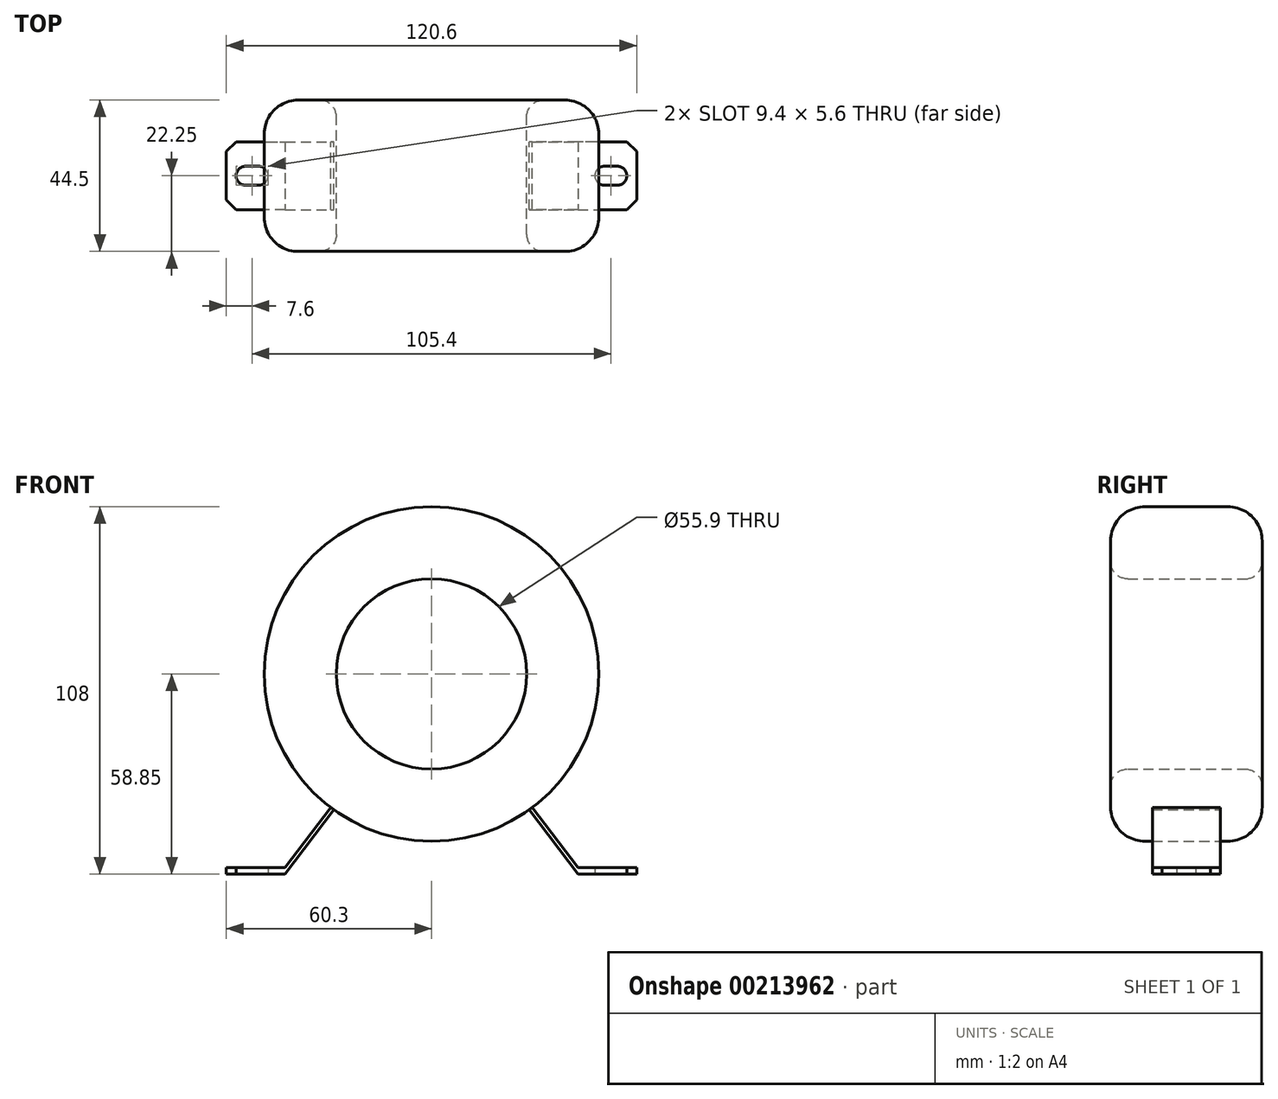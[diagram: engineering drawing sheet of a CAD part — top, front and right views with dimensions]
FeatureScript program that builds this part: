
annotation { "Feature Type Name" : "Feature", "Feature Type Description" : "" }
export const myFeature = defineFeature(function(context is Context, id is Id, definition is map)
    precondition{}
    {
        {
            var Q0;
            Q0=qCreatedBy(makeId("Front.planeOp"),FACE);
            var sketch = newSketch(context, id + "F0", { "sketchPlane" : qUnion([Q0])});
            skCircle(sketch, "E0", {"center": v(0, 49.15) * mm, "radius": 27.95 * mm});
            skCircle(sketch, "E1", {"center": v(0, 49.15) * mm, "radius": 49.15 * mm});
            skPoint(sketch, "E2", {"position": v(0, 0) * mm});
            skPoint(sketch, "E3", {"position": v(0, 21.2) * mm});
            skLineSegment(sketch, "E4", {"start": v(-76.83, -9.7) * mm, "end": v(67.55, -9.7) * mm});
            skSolve(sketch);
        }
        {
            var Q0;
            Q0=makeQuery(id+"F0.imprint","IMPRINT",FACE,{"disambiguationData":[TD([[makeQuery(id+"F0.imprint","IMPRINT",EDGE,{"derivedFrom":sQuery(id+"F0.wireOp",EDGE,"E0")}),-1.0]])]});
            extrude(context, id + "F1", {"entities" : qUnion([Q0]), "endBound" : BoundingType.SYMMETRIC, "depth" : 44.5 * mm});
        }
        {
            var Q0;
            Q0=makeQuery(id+"F1.opExtrude","CAP_EDGE",EDGE,{"disambiguationData":[OSD([sQuery(id+"F0.wireOp",EDGE,"E1")])],"isStart":false});
            var Q1;
            Q1=makeQuery(id+"F1.opExtrude","CAP_EDGE",EDGE,{"disambiguationData":[OSD([sQuery(id+"F0.wireOp",EDGE,"E1")])],"isStart":true});
            fillet(context, id + "F2", {"entities" : qUnion([Q0, Q1]), "radius" : 10 * mm, "tangentPropagation" : true, "allowEdgeOverflow" : false});
        }
        {
            var Q0;
            Q0=makeQuery(id+"F1.opExtrude","CAP_EDGE",EDGE,{"disambiguationData":[OSD([sQuery(id+"F0.wireOp",EDGE,"E0")])],"isStart":true});
            var Q1;
            Q1=makeQuery(id+"F1.opExtrude","CAP_EDGE",EDGE,{"disambiguationData":[OSD([sQuery(id+"F0.wireOp",EDGE,"E0")])],"isStart":false});
            fillet(context, id + "F3", {"entities" : qUnion([Q0, Q1]), "radius" : 5 * mm, "tangentPropagation" : true, "allowEdgeOverflow" : false});
        }
        {
            var Q0;
            Q0=sQuery(id+"F0.wireOp",EDGE,"E4");
            extrude(context, id + "F4", {"bodyType" : ToolBodyType.SURFACE, "surfaceEntities" : qUnion([Q0]), "endBound" : BoundingType.SYMMETRIC, "depth" : 25 * mm});
        }
        {
            var Q0;
            Q0=makeQuery(id+"F4.opExtrude","SWEPT_FACE",FACE,{"disambiguationData":[OSD([sQuery(id+"F0.wireOp",EDGE,"E4")])]});
            var sketch = newSketch(context, id + "F5", { "sketchPlane" : qUnion([Q0])});
            skLineSegment(sketch, "E5", {"start": v(0, -24.95) * mm, "end": v(0, 24.95) * mm, "construction": true});
            skLineSegment(sketch, "E6", {"start": v(-57.4, 0) * mm, "end": v(57.4, 0) * mm, "construction": true});
            skLineSegment(sketch, "E7", {"start": v(43, -10) * mm, "end": v(43, 10) * mm});
            skLineSegment(sketch, "E8", {"start": v(43, 10) * mm, "end": v(57.4, 10) * mm});
            skLineSegment(sketch, "E9", {"start": v(57.4, 10) * mm, "end": v(60.3, 7.1) * mm});
            skLineSegment(sketch, "E10", {"start": v(60.3, 7.1) * mm, "end": v(60.3, -7.1) * mm});
            skLineSegment(sketch, "E11", {"start": v(60.3, -7.1) * mm, "end": v(57.4, -10) * mm});
            skLineSegment(sketch, "E12", {"start": v(57.4, -10) * mm, "end": v(43, -10) * mm});
            skCircle(sketch, "E13", {"center": v(54.6, 0) * mm, "radius": 2.8 * mm});
            skCircle(sketch, "E14", {"center": v(50.8, 0) * mm, "radius": 2.8 * mm});
            skLineSegment(sketch, "E15", {"start": v(50.8, -2.8) * mm, "end": v(54.6, -2.8) * mm});
            skLineSegment(sketch, "E16", {"start": v(54.6, 2.8) * mm, "end": v(50.8, 2.8) * mm});
            skLineSegment(sketch, "E17.MirrorCS", {"start": v(-43, -10) * mm, "end": v(-43, 10) * mm});
            skLineSegment(sketch, "E18.MirrorCS", {"start": v(-57.4, -10) * mm, "end": v(-43, -10) * mm});
            skLineSegment(sketch, "E19.MirrorCS", {"start": v(-60.3, -7.1) * mm, "end": v(-57.4, -10) * mm});
            skLineSegment(sketch, "E20.MirrorCS", {"start": v(-60.3, 7.1) * mm, "end": v(-60.3, -7.1) * mm});
            skLineSegment(sketch, "E21.MirrorCS", {"start": v(-57.4, 10) * mm, "end": v(-60.3, 7.1) * mm});
            skLineSegment(sketch, "E22.MirrorCS", {"start": v(-43, 10) * mm, "end": v(-57.4, 10) * mm});
            skCircle(sketch, "E23.MirrorC", {"center": v(-54.6, 0) * mm, "radius": 2.8 * mm});
            skCircle(sketch, "E24.MirrorC", {"center": v(-50.8, 0) * mm, "radius": 2.8 * mm});
            skLineSegment(sketch, "E25.MirrorCS", {"start": v(-54.6, 2.8) * mm, "end": v(-50.8, 2.8) * mm});
            skLineSegment(sketch, "E26.MirrorCS", {"start": v(-50.8, -2.8) * mm, "end": v(-54.6, -2.8) * mm});
            skSolve(sketch);
        }
        {
            var Q0;
            Q0=makeQuery(id+"F4.opExtrude","SWEPT_BODY",BODY,{"disambiguationData":[OSD([sQuery(id+"F0.wireOp",EDGE,"E4")])]});
            deleteBodies(context, id + "F6", {"entities" : qUnion([Q0])});
        }
        {
            var Q0;
            Q0=makeQuery(id+"F5.imprint","IMPRINT",FACE,{"disambiguationData":[TD([[makeQuery(id+"F5.imprint","IMPRINT",EDGE,{"derivedFrom":sQuery(id+"F5.wireOp",EDGE,"E7")}),-1.0]])]});
            var Q1;
            Q1=makeQuery(id+"F5.imprint","IMPRINT",FACE,{"disambiguationData":[TD([[makeQuery(id+"F5.imprint","IMPRINT",EDGE,{"derivedFrom":sQuery(id+"F5.wireOp",EDGE,"E17.MirrorCS")}),1.0]])]});
            extrude(context, id + "F7", {"entities" : qUnion([Q0, Q1]), "oppositeDirection" : true, "depth" : 2 * mm});
        }
        {
            var Q0;
            Q0=makeQuery(id+"F7.opExtrude","SWEPT_FACE",FACE,{"disambiguationData":[OSD([sQuery(id+"F5.wireOp",EDGE,"E12")])]});
            var sketch = newSketch(context, id + "F8", { "sketchPlane" : qUnion([Q0])});
            skCircle(sketch, "E27.0", {"center": v(0, 49.15) * mm, "radius": 49.15 * mm});
            skLineSegment(sketch, "E28", {"start": v(-29.65, 9.95) * mm, "end": v(-43, -7.7) * mm});
            skLineSegment(sketch, "E29", {"start": v(-43, -9.7) * mm, "end": v(-28.68, 9.23) * mm});
            skPoint(sketch, "E30.0", {"position": v(43, -7.7) * mm});
            skPoint(sketch, "E30.1", {"position": v(43, -9.7) * mm});
            skLineSegment(sketch, "E31", {"start": v(43, -7.7) * mm, "end": v(29.65, 9.95) * mm});
            skLineSegment(sketch, "E32", {"start": v(43, -9.7) * mm, "end": v(28.68, 9.23) * mm});
            skLineSegment(sketch, "E33.0", {"start": v(43, -7.7) * mm, "end": v(43, -9.7) * mm});
            skSolve(sketch);
        }
        {
            var Q0;
            {var subQ0=sQuery(id+"F8.wireOp",EDGE,"E31");Q0=makeQuery(id+"F8.imprint","IMPRINT",FACE,{"disambiguationData":[TD([[makeQuery(id+"F8.imprint","IMPRINT",EDGE,{"derivedFrom":subQ0}),1.0]])]});}
            var Q1;
            {var subQ0=sQuery(id+"F8.wireOp",EDGE,"E28");Q1=makeQuery(id+"F8.imprint","IMPRINT",FACE,{"disambiguationData":[TD([[makeQuery(id+"F8.imprint","IMPRINT",EDGE,{"derivedFrom":subQ0}),1.0]])]});}
            var Q2;
            Q2=makeQuery(id+"F7.opExtrude","SWEPT_FACE",FACE,{"disambiguationData":[OSD([sQuery(id+"F5.wireOp",EDGE,"E22.MirrorCS")])]});
            extrude(context, id + "F9", {"entities" : qUnion([Q0, Q1]), "operationType" : NewBodyOperationType.ADD, "endBound" : BoundingType.UP_TO_SURFACE, "oppositeDirection" : true, "endBoundEntityFace" : qUnion([Q2]), "depth" : 25 * mm});
        }
    });
